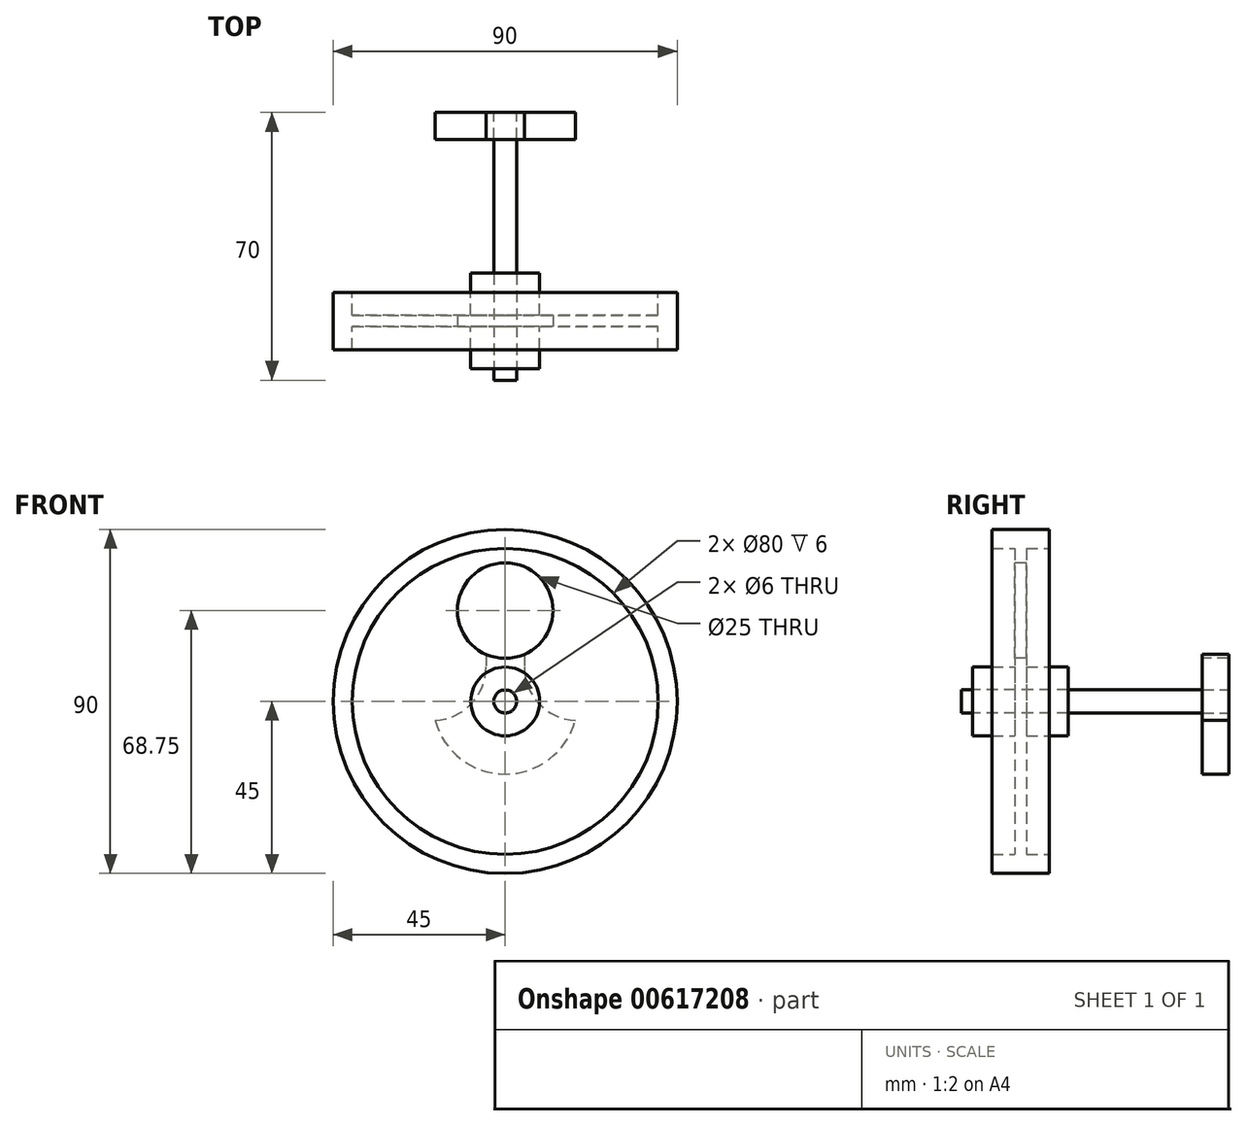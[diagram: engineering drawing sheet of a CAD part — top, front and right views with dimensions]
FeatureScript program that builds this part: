
annotation { "Feature Type Name" : "Feature", "Feature Type Description" : "" }
export const myFeature = defineFeature(function(context is Context, id is Id, definition is map)
    precondition{}
    {
        {
            var Q0;
            Q0=qCreatedBy(makeId("Front.planeOp"),FACE);
            var sketch = newSketch(context, id + "F0", { "sketchPlane" : qUnion([Q0])});
            skArc(sketch, "E0", {"start": v(5, 18.33) * mm, "mid": v(0, 19) * mm, "end": v(-5, 18.33) * mm});
            skLineSegment(sketch, "E1", {"start": v(-5, 18.33) * mm, "end": v(-5, 9) * mm});
            skArc(sketch, "E2", {"start": v(-5, 9) * mm, "mid": v(-8.87, -0.66) * mm, "end": v(-18.33, -4.98) * mm});
            skLineSegment(sketch, "E3", {"start": v(0, 0) * mm, "end": v(0, 19) * mm, "construction": true});
            skLineSegment(sketch, "E4.MirrorCS", {"start": v(5, 18.33) * mm, "end": v(5, 9) * mm});
            skArc(sketch, "E5.MirrorCS", {"start": v(5, 9) * mm, "mid": v(8.87, -0.66) * mm, "end": v(18.33, -4.98) * mm});
            skArc(sketch, "E6.trimOffspring", {"start": v(-18.33, -4.98) * mm, "mid": v(0, -19) * mm, "end": v(18.33, -4.98) * mm});
            skPoint(sketch, "E7", {"position": v(0, 14) * mm});
            skSolve(sketch);
        }
        {
            var Q0;
            Q0 = qSketchRegion(id + "F0", true);
            extrude(context, id + "F1", {"entities" : qUnion([Q0]), "depth" : 7 * mm, "offsetDistance" : 25 * mm});
        }
        {
            var Q0;
            Q0=sQuery(id+"F0.wireOp",VERTEX,"E0.center");
            var Q1;
            Q1=makeQuery(id+"F1.opExtrude","SWEPT_BODY",BODY,{"disambiguationData":[OSD([sQuery(id+"F0.wireOp",EDGE,"E0"),sQuery(id+"F0.wireOp",EDGE,"E1"),sQuery(id+"F0.wireOp",EDGE,"E2"),sQuery(id+"F0.wireOp",EDGE,"E4.MirrorCS"),sQuery(id+"F0.wireOp",EDGE,"E5.MirrorCS"),sQuery(id+"F0.wireOp",EDGE,"E6.trimOffspring")])]});
            hole(context, id + "F2", {"style" : HoleStyle.SIMPLE, "endStyle" : HoleEndStyle.THROUGH, "oppositeDirection" : true, "standardTappedOrClearance" : lookupTablePath({ "standard" : "ISO", "size" : "6", "type" : "Drilled" }), "standardBlindInLast" : lookupTablePath({ "standard" : "ISO", "size" : "6", "type" : "Drilled" }), "holeDiameter" : 6 * mm, "majorDiameter" : 5 * mm, "isTappedThrough" : true, "tappedDepth" : 6 * mm, "tapClearance" : 2, "locations" : qUnion([Q0]), "scope" : qUnion([Q1])});
        }
        {
            var Q0;
            Q0=sQuery(id+"F0.wireOp",VERTEX,"E7");
            var Q1;
            Q1=makeQuery(id+"F1.opExtrude","SWEPT_BODY",BODY,{"disambiguationData":[OSD([sQuery(id+"F0.wireOp",EDGE,"E0"),sQuery(id+"F0.wireOp",EDGE,"E1"),sQuery(id+"F0.wireOp",EDGE,"E2"),sQuery(id+"F0.wireOp",EDGE,"E4.MirrorCS"),sQuery(id+"F0.wireOp",EDGE,"E5.MirrorCS"),sQuery(id+"F0.wireOp",EDGE,"E6.trimOffspring")])]});
            hole(context, id + "F3", {"style" : HoleStyle.SIMPLE, "endStyle" : HoleEndStyle.THROUGH, "oppositeDirection" : true, "standardTappedOrClearance" : lookupTablePath({ "standard" : "ISO", "engagement" : "75%", "pitch" : "0.7 mm", "size" : "M4", "type" : "Tapped" }), "standardBlindInLast" : lookupTablePath({ "standard" : "ISO", "engagement" : "75%", "pitch" : "0.7 mm", "size" : "M4", "type" : "Tapped" }), "holeDiameter" : 3.3 * mm, "majorDiameter" : 4 * mm, "showTappedDepth" : true, "isTappedThrough" : true, "tappedDepth" : 6 * mm, "tapClearance" : 2, "locations" : qUnion([Q0]), "scope" : qUnion([Q1])});
        }
        {
            var Q0;
            Q0=makeQuery(id+"F1.opExtrude","CAP_FACE",FACE,{"disambiguationData":[OSD([sQuery(id+"F0.wireOp",EDGE,"E0"),sQuery(id+"F0.wireOp",EDGE,"E1"),sQuery(id+"F0.wireOp",EDGE,"E2"),sQuery(id+"F0.wireOp",EDGE,"E4.MirrorCS"),sQuery(id+"F0.wireOp",EDGE,"E5.MirrorCS"),sQuery(id+"F0.wireOp",EDGE,"E6.trimOffspring")])],"isStart":true});
            var sketch = newSketch(context, id + "F4", { "sketchPlane" : qUnion([Q0])});
            skCircle(sketch, "E8", {"center": v(0, 14) * mm, "radius": 2.5 * mm});
            skSolve(sketch);
        }
        {
            var Q0;
            Q0 = qSketchRegion(id + "F4", true);
            extrude(context, id + "F5", {"entities" : qUnion([Q0]), "depth" : 9 * mm, "offsetDistance" : 25 * mm});
        }
        {
            var Q0;
            Q0=makeQuery(id+"F5.opExtrude","CAP_FACE",FACE,{"disambiguationData":[OSD([sQuery(id+"F4.wireOp",EDGE,"E8")])],"isStart":true});
            var sketch = newSketch(context, id + "F6", { "sketchPlane" : qUnion([Q0])});
            skCircle(sketch, "E9", {"center": v(0, 14) * mm, "radius": 2 * mm});
            skSolve(sketch);
        }
        {
            var Q0;
            Q0 = qSketchRegion(id + "F6", true);
            extrude(context, id + "F7", {"entities" : qUnion([Q0]), "operationType" : NewBodyOperationType.ADD, "depth" : 7 * mm, "offsetDistance" : 25 * mm});
        }
        {
            var Q0;
            Q0=makeQuery(id+"F5.opExtrude","CAP_FACE",FACE,{"disambiguationData":[OSD([sQuery(id+"F4.wireOp",EDGE,"E8")])],"isStart":false});
            var sketch = newSketch(context, id + "F8", { "sketchPlane" : qUnion([Q0])});
            skCircle(sketch, "E10", {"center": v(0, 14) * mm, "radius": 1.5 * mm});
            skSolve(sketch);
        }
        {
            var Q0;
            Q0 = qSketchRegion(id + "F8", true);
            extrude(context, id + "F9", {"entities" : qUnion([Q0]), "operationType" : NewBodyOperationType.ADD, "depth" : 3 * mm, "offsetDistance" : 25 * mm});
        }
        {
            var Q0;
            Q0=makeQuery(id+"F9.opExtrude","CAP_EDGE",EDGE,{"disambiguationData":[OSD([sQuery(id+"F8.wireOp",EDGE,"E10")])],"isStart":false});
            var Q1;
            Q1=makeQuery(id+"F7.opExtrude","CAP_EDGE",EDGE,{"disambiguationData":[OSD([sQuery(id+"F6.wireOp",EDGE,"E9")])],"isStart":false});
            chamfer(context, id + "F10", {"entities" : qUnion([Q0, Q1]), "width" : .5 * mm, "tangentPropagation" : true});
        }
        {
            var Q0;
            Q0=qCreatedBy(makeId("Front.planeOp"),FACE);
            var sketch = newSketch(context, id + "F11", { "sketchPlane" : qUnion([Q0])});
            skCircle(sketch, "E11", {"center": v(0, 0) * mm, "radius": 3 * mm});
            skSolve(sketch);
        }
        {
            var Q0;
            Q0 = qSketchRegion(id + "F11", true);
            extrude(context, id + "F12", {"entities" : qUnion([Q0]), "depth" : 70 * mm, "offsetDistance" : 25 * mm});
        }
        {
            var Q0;
            Q0=qCreatedBy(makeId("Top.planeOp"),FACE);
            var sketch = newSketch(context, id + "F13", { "sketchPlane" : qUnion([Q0])});
            skLineSegment(sketch, "E12", {"start": v(0, -32.63) * mm, "end": v(0, -93.54) * mm, "construction": true});
            skLineSegment(sketch, "E13", {"start": v(0, -67) * mm, "end": v(9, -67) * mm});
            skLineSegment(sketch, "E14", {"start": v(9, -67) * mm, "end": v(9, -56) * mm});
            skLineSegment(sketch, "E15", {"start": v(40, -62) * mm, "end": v(45, -62) * mm});
            skLineSegment(sketch, "E16", {"start": v(45, -62) * mm, "end": v(45, -47) * mm});
            skLineSegment(sketch, "E17", {"start": v(45, -47) * mm, "end": v(40, -47) * mm});
            skLineSegment(sketch, "E18", {"start": v(9, -53) * mm, "end": v(9, -42) * mm});
            skLineSegment(sketch, "E19", {"start": v(9, -42) * mm, "end": v(0, -42) * mm});
            skLineSegment(sketch, "E20", {"start": v(0, -42) * mm, "end": v(0, -67) * mm});
            skLineSegment(sketch, "E21", {"start": v(40, -62) * mm, "end": v(40, -56) * mm});
            skLineSegment(sketch, "E22", {"start": v(40, -56) * mm, "end": v(9, -56) * mm});
            skLineSegment(sketch, "E23", {"start": v(40, -47) * mm, "end": v(40, -53) * mm});
            skLineSegment(sketch, "E24", {"start": v(40, -53) * mm, "end": v(9, -53) * mm});
            skSolve(sketch);
        }
        {
            var Q0;
            Q0 = qSketchRegion(id + "F13", true);
            var Q1;
            Q1=sQuery(id+"F13.wireOp",EDGE,"E12");
            revolve(context, id + "F14", {"entities" : qUnion([Q0]), "axis" : qUnion([Q1]), "revolveType" : RevolveType.FULL});
        }
        {
            var Q0;
            Q0=makeQuery(id+"F14.opRevolve","SWEPT_FACE",FACE,{"disambiguationData":[OSD([sQuery(id+"F13.wireOp",EDGE,"E13")])]});
            var sketch = newSketch(context, id + "F15", { "sketchPlane" : qUnion([Q0])});
            skPoint(sketch, "E25", {"position": v(0, 0) * mm});
            skSolve(sketch);
        }
        {
            var Q0;
            Q0=sQuery(id+"F15.wireOp",VERTEX,"E25");
            var Q1;
            Q1=makeQuery(id+"F14.opRevolve","SWEPT_BODY",BODY,{"disambiguationData":[OSD([sQuery(id+"F13.wireOp",EDGE,"E13"),sQuery(id+"F13.wireOp",EDGE,"E14"),sQuery(id+"F13.wireOp",EDGE,"E15"),sQuery(id+"F13.wireOp",EDGE,"E16"),sQuery(id+"F13.wireOp",EDGE,"E17"),sQuery(id+"F13.wireOp",EDGE,"E18"),sQuery(id+"F13.wireOp",EDGE,"E19"),sQuery(id+"F13.wireOp",EDGE,"E20")])]});
            hole(context, id + "F16", {"style" : HoleStyle.SIMPLE, "endStyle" : HoleEndStyle.THROUGH, "standardTappedOrClearance" : lookupTablePath({ "standard" : "ISO", "size" : "6", "type" : "Drilled" }), "standardBlindInLast" : lookupTablePath({ "standard" : "ISO", "size" : "6", "type" : "Drilled" }), "holeDiameter" : 6 * mm, "majorDiameter" : 3 * mm, "isTappedThrough" : true, "tappedDepth" : 6 * mm, "tapClearance" : 2, "locations" : qUnion([Q0]), "scope" : qUnion([Q1])});
        }
        {
            var Q0;
            Q0=makeQuery(id+"F14.opRevolve","SWEPT_FACE",FACE,{"disambiguationData":[OSD([sQuery(id+"F13.wireOp",EDGE,"E22")])]});
            var sketch = newSketch(context, id + "F17", { "sketchPlane" : qUnion([Q0])});
            skCircle(sketch, "E26", {"center": v(0, 23.75) * mm, "radius": 12.5 * mm});
            skCircle(sketch, "E27", {"center": v(0, 0) * mm, "radius": 23.75 * mm, "construction": true});
            skSolve(sketch);
        }
        {
            var Q0;
            Q0 = qSketchRegion(id + "F17", true);
            extrude(context, id + "F18", {"entities" : qUnion([Q0]), "operationType" : NewBodyOperationType.REMOVE, "endBound" : BoundingType.THROUGH_ALL, "oppositeDirection" : true, "depth" : 25 * mm, "offsetDistance" : 25 * mm});
        }
    });
